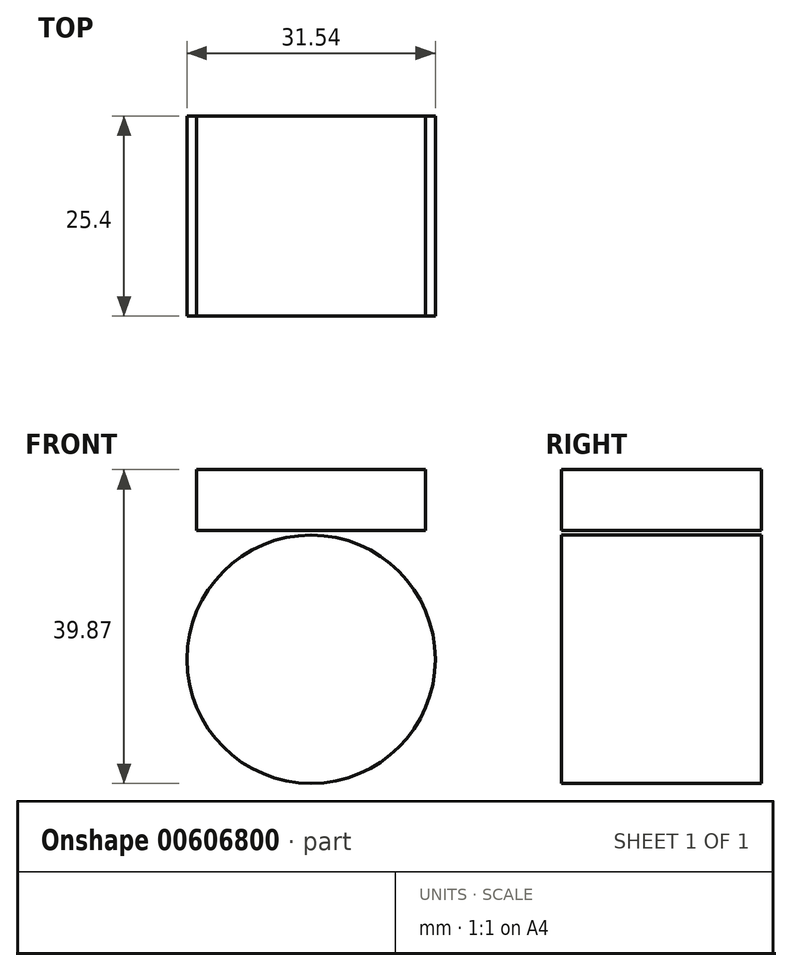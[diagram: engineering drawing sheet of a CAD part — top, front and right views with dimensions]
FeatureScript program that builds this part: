
annotation { "Feature Type Name" : "Feature", "Feature Type Description" : "" }
export const myFeature = defineFeature(function(context is Context, id is Id, definition is map)
    precondition{}
    {
        {
            var Q0;
            Q0=qCreatedBy(makeId("Front.planeOp"),FACE);
            var sketch = newSketch(context, id + "F0", { "sketchPlane" : qUnion([Q0])});
            skCircle(sketch, "E0", {"center": v(-33.43, 17.74) * mm, "radius": 15.77 * mm});
            skLineSegment(sketch, "E1.bottom", {"start": v(-47.98, 41.84) * mm, "end": v(-18.88, 41.84) * mm});
            skLineSegment(sketch, "E1.top", {"start": v(-47.98, 34.11) * mm, "end": v(-18.88, 34.11) * mm});
            skLineSegment(sketch, "E1.left", {"start": v(-47.98, 41.84) * mm, "end": v(-47.98, 34.11) * mm});
            skLineSegment(sketch, "E1.right", {"start": v(-18.88, 41.84) * mm, "end": v(-18.88, 34.11) * mm});
            skSolve(sketch);
        }
        {
            var Q0;
            Q0 = qSketchRegion(id + "F0", true);
            extrude(context, id + "F1", {"entities" : qUnion([Q0]), "depth" : 25.4 * mm, "offsetDistance" : 25.4 * mm});
        }
    });
